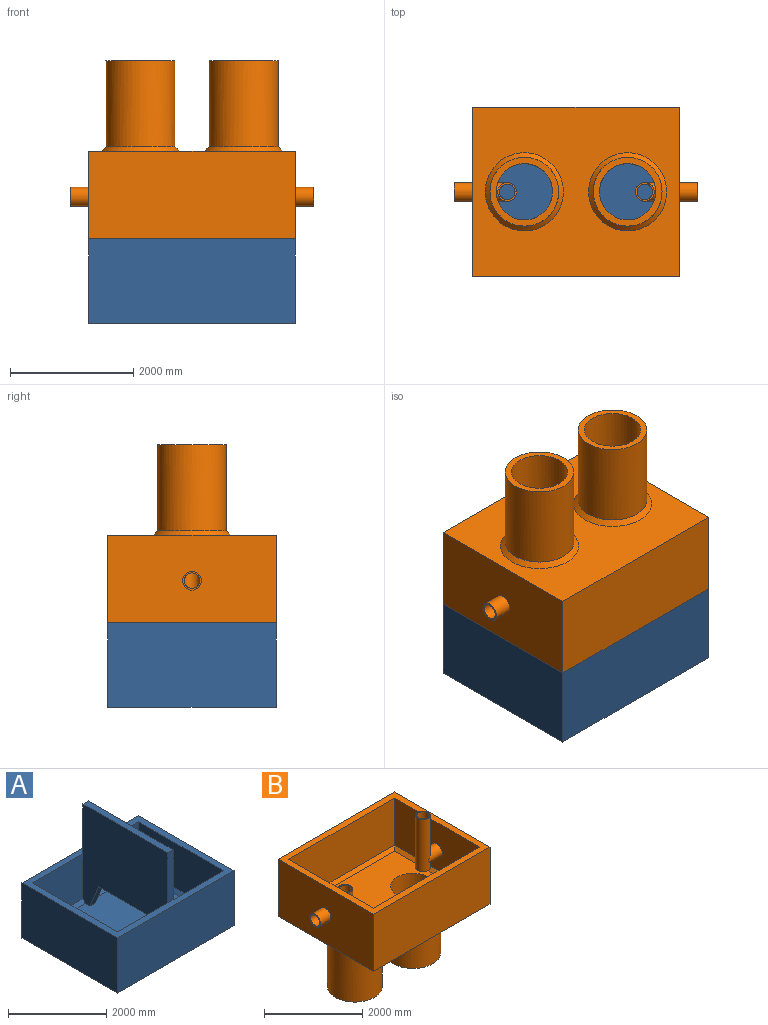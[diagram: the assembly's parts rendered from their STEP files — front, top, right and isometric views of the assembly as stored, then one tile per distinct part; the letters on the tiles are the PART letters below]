
ASSEMBLY  parts=2 mates=1
PART A: 27 faces, bbox 3352.8x2743.2x2616.2 mm
  f0: plane 1447.8x1117.6mm, normal (0,-1,0), area 1618061.3mm2, adj f8,f12,f20,f24
  f1: plane 1447.8x1117.6mm, normal (0,1,0), area 1618061.3mm2, adj f8,f12,f20,f26
  f2: plane 2895.6x2286mm, normal (0,0,1), area 6580632mm2, adj f15,f17,f19,f20,f21,f22,f23,f24
  f3: plane 2743.2x1371.6mm, normal (-1,0,0), area 3762573.1mm2, adj f4,f6,f7,f12
  f4: plane 3352.8x1371.6mm, normal (0,-1,0), area 4598700.5mm2, adj f3,f5,f7,f12
  f5: plane 2743.2x1371.6mm, normal (1,0,0), area 3762573.1mm2, adj f4,f6,f7,f12
  f6: plane 3352.8x1371.6mm, normal (0,1,0), area 4598700.5mm2, adj f3,f5,f7,f12
  f7: plane 3352.8x2743.2mm, normal (0,0,-1), area 9197401mm2, adj f3,f4,f5,f6
  f8: plane 2438.4x1117.6mm, normal (1,0,0), area 2725155.8mm2, adj f0,f1,f12,f25
  f9: plane 1447.8x1117.6mm, normal (0,-1,0), area 1618061.3mm2, adj f10,f12,f19,f22
  f10: plane 2438.4x1117.6mm, normal (-1,0,0), area 2725155.8mm2, adj f9,f11,f12,f23
  f11: plane 1447.8x1117.6mm, normal (0,1,0), area 1618061.3mm2, adj f10,f12,f19,f21
  f12: plane 3352.8x2743.2mm, normal (0,0,1), area 1765157.8mm2, adj f0,f1,f3,f4,f5,f6,f8,f9
  f13: plane 1244.6x152.4mm, normal (0,1,0), area 189677mm2, adj f12,f16,f19,f20
  f14: plane 1244.6x152.4mm, normal (0,-1,0), area 189677mm2, adj f12,f16,f19,f20
  f15: plane 609.6x254mm, normal (0,-0.92,-0.38), area 100645mm2, adj f2,f18,f19,f20
  f16: plane 2438.4x152.4mm, normal (0,0,1), area 371612.2mm2, adj f13,f14,f19,f20
  f17: plane 609.6x254mm, normal (0,0.92,-0.38), area 100645mm2, adj f2,f18,f19,f20
  f18: plane 1524x152.4mm, normal (0,0,-1), area 232257.6mm2, adj f15,f17,f19,f20
  f19: plane 2438.4x2438.4mm, normal (1,0,0), area 4856119.3mm2, adj f2,f9,f11,f13,f14,f15,f16,f17
  f20: plane 2438.4x2438.4mm, normal (-1,0,0), area 4856119.3mm2, adj f0,f1,f2,f13,f14,f15,f16,f17
  f21: plane 1447.8x76.2mm, normal (0,0.71,0.71), area 151913.6mm2, adj f2,f11,f19,f23
  f22: plane 1447.8x76.2mm, normal (0,-0.71,0.71), area 151913.6mm2, adj f2,f9,f19,f23
  f23: plane 2438.4x76.2mm, normal (-0.71,0,0.71), area 254557.9mm2, adj f2,f10,f21,f22
  f24: plane 1447.8x76.2mm, normal (0,-0.71,0.71), area 151913.6mm2, adj f0,f2,f20,f25
  f25: plane 2438.4x76.2mm, normal (0.71,0,0.71), area 254557.9mm2, adj f2,f8,f24,f26
  f26: plane 1447.8x76.2mm, normal (0,0.71,0.71), area 151913.6mm2, adj f1,f2,f20,f25
PART B: 39 faces, bbox 3962.4x2743.2x3276.6 mm
  f0: cylinder r=127mm len=1295.4mm, axis (0,0,-1), area 969167.3mm2, adj f1,f35,f36
  f1: cylinder r=127mm len=863.6mm, axis (-1,0,0), area 624606.2mm2, adj f0,f21
  f2: cylinder r=152.4mm len=406.4mm, axis (1,0,0), area 296248.3mm2, adj f12,f37
  f3: cylinder r=127mm len=863.6mm, axis (-1,0,0), area 624606.2mm2, adj f31,f38
  f4: cylinder r=152.4mm len=406.4mm, axis (-1,0,0), area 296248.3mm2, adj f10,f34
  f5: plane 2743.2x1422.4mm, normal (-1,0,0), area 3828961.8mm2, adj f6,f8,f9,f14,f30
  f6: plane 3352.8x1422.4mm, normal (0,-1,0), area 4769022.7mm2, adj f5,f7,f9,f14
  f7: plane 2743.2x1422.4mm, normal (1,0,0), area 3828961.8mm2, adj f6,f8,f9,f14,f20
  f8: plane 3352.8x1422.4mm, normal (0,1,0), area 4769022.7mm2, adj f5,f7,f9,f14
  f9: plane 3352.8x2743.2mm, normal (0,0,-1), area 6663863.6mm2, adj f5,f6,f7,f8,f28,f29
  f10: plane 2438.4x1168.4mm, normal (1,0,0), area 2776060.7mm2, adj f4,f11,f13,f14,f16
  f11: plane 3048x1168.4mm, normal (0,-1,0), area 3561283.2mm2, adj f10,f12,f14,f18
  f12: plane 2438.4x1168.4mm, normal (-1,0,0), area 2776060.7mm2, adj f2,f11,f13,f14,f19
  f13: plane 3048x1168.4mm, normal (0,1,0), area 3561283.2mm2, adj f10,f12,f14,f17
  f14: plane 3352.8x2743.2mm, normal (0,0,1), area 1765157.8mm2, adj f5,f6,f7,f8,f10,f11,f12,f13
  f15: plane 2895.6x2286mm, normal (0,0,1), area 5305955.8mm2, adj f16,f17,f18,f19,f22,f25
  f16: plane 2438.4x76.2mm, normal (0.71,0,0.71), area 254557.9mm2, adj f10,f15,f17,f18
  f17: plane 3048x76.2mm, normal (0,0.71,0.71), area 320250.3mm2, adj f13,f15,f16,f19
  f18: plane 3048x76.2mm, normal (0,-0.71,0.71), area 320250.3mm2, adj f11,f15,f16,f19
  f19: plane 2438.4x76.2mm, normal (-0.71,0,0.71), area 254557.9mm2, adj f12,f15,f17,f18
  f20: cylinder r=152.4mm len=304.8mm, axis (-1,0,0), area 291863.5mm2, adj f7,f21
  f21: plane 304.8x304.8mm, normal (1,0,0), area 22295.1mm2, adj f1,f20
  f22: cylinder r=457.2mm len=1651mm, axis (0,0,1), area 4742782mm2, adj f15,f24
  f23: cylinder r=558.8mm len=1397mm, axis (0,0,1), area 4904928.4mm2, adj f24,f29
  f24: plane 1117.6x1117.6mm, normal (0,0,-1), area 324292.8mm2, adj f22,f23
  f25: cylinder r=457.2mm len=1651mm, axis (0,0,1), area 4742782mm2, adj f15,f27
  f26: cylinder r=558.8mm len=1397mm, axis (0,0,1), area 4904928.4mm2, adj f27,f28
  f27: plane 1117.6x1117.6mm, normal (0,0,-1), area 324292.8mm2, adj f25,f26
  f28: cone r=558.8mm half-angle=45deg, axis (0,0,1), area 404158.2mm2, adj f9,f26
  f29: cone r=558.8mm half-angle=45deg, axis (0,0,1), area 404158.2mm2, adj f9,f23
  f30: cylinder r=152.4mm len=304.8mm, axis (1,0,0), area 291863.5mm2, adj f5,f31
  f31: plane 304.8x304.8mm, normal (-1,0,0), area 22295.1mm2, adj f3,f30
  f32: plane 304.8x304.8mm, normal (0,0,-1), area 22295.1mm2, adj f34,f38
  f33: plane 304.8x304.8mm, normal (0,0,1), area 22295.1mm2, adj f34,f38
  f34: cylinder r=152.4mm len=584.2mm, axis (0,0,-1), area 466502.1mm2, adj f4,f32,f33
  f35: plane 304.8x304.8mm, normal (0,0,-1), area 22295.1mm2, adj f0,f37
  f36: plane 304.8x304.8mm, normal (0,0,1), area 22295.1mm2, adj f0,f37
  f37: cylinder r=152.4mm len=1295.4mm, axis (0,0,-1), area 1147516.9mm2, adj f2,f35,f36
  f38: cylinder r=127mm len=584.2mm, axis (0,0,-1), area 401654.9mm2, adj f3,f32,f33
PLACE A at identity fixed
PLACE B rot(axis=(1,0,0),180deg) t=(0,2743.2,2794)mm
MATE fastened A.f12 <-> B.f14  axis (0,0,1) through (0,0,1371.6)mm
